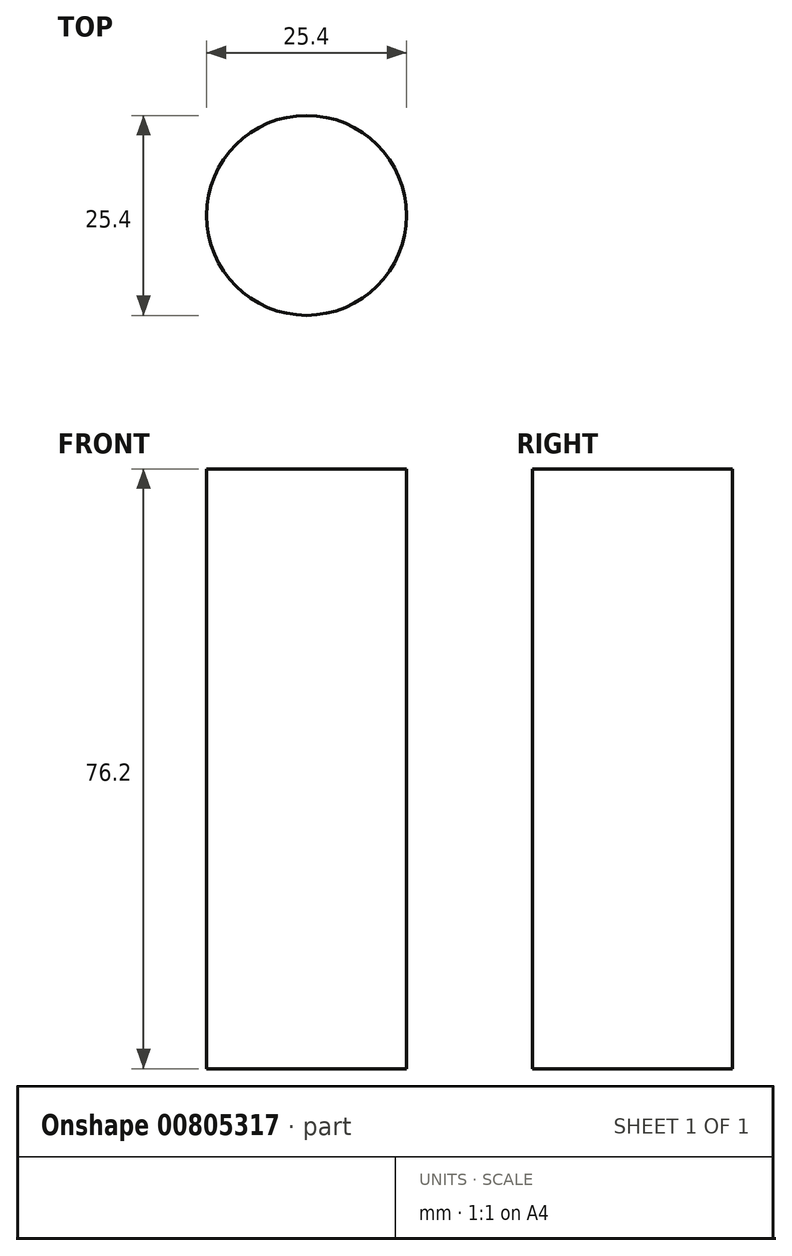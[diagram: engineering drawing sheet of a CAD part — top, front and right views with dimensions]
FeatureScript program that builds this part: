
annotation { "Feature Type Name" : "Feature", "Feature Type Description" : "" }
export const myFeature = defineFeature(function(context is Context, id is Id, definition is map)
    precondition{}
    {
        {
            var Q0;
            Q0=qCreatedBy(makeId("Front.planeOp"),FACE);
            var sketch = newSketch(context, id + "F0", { "sketchPlane" : qUnion([Q0])});
            skLineSegment(sketch, "E0", {"start": v(0, 0) * mm, "end": v(88.9, 0) * mm});
            skLineSegment(sketch, "E1", {"start": v(88.9, 0) * mm, "end": v(88.9, 1092.2) * mm});
            skLineSegment(sketch, "E2", {"start": v(88.9, 1092.2) * mm, "end": v(0, 1092.2) * mm});
            skLineSegment(sketch, "E3", {"start": v(0, 0) * mm, "end": v(0, 1191.58) * mm, "construction": true});
            skSolve(sketch);
        }
        {
            var Q0;
            Q0=qSketchRegion(id+"F0",true);
            var Q1;
            Q1=sQuery(id+"F0.wireOp",EDGE,"E1");
            var Q2;
            Q2=sQuery(id+"F0.wireOp",EDGE,"E0");
            var Q3;
            Q3=sQuery(id+"F0.wireOp",EDGE,"E2");
            var Q4;
            Q4=sQuery(id+"F0.wireOp",EDGE,"Eqfm1BcG-SU4s-36cT-mnSU-gtJC7Ga610LP");
            var Q5;
            Q5=sQuery(id+"F0.wireOp",EDGE,"Ojjtict1-wwqD-w4ix-8k3J-fVzUUkNspiEs");
            var Q6;
            Q6=sQuery(id+"F0.wireOp",EDGE,"E3");
            revolve(context, id + "F1", {"bodyType" : ToolBodyType.SURFACE, "entities" : qUnion([Q0]), "surfaceEntities" : qUnion([Q1, Q2, Q3, Q4, Q5]), "axis" : qUnion([Q6]), "revolveType" : RevolveType.FULL});
        }
        {
            var Q0;
            Q0=makeQuery(id+"F1.opRevolve","SWEPT_EDGE",EDGE,{"disambiguationData":[OSD([sQuery(id+"F0.wireOp",VERTEX,"E2.start")])]});
            fillet(context, id + "F2", {"entities" : qUnion([Q0]), "radius" : 76.2 * mm, "tangentPropagation" : true, "allowEdgeOverflow" : false});
        }
        {
            var Q0;
            Q0=makeQuery(id+"F1.opRevolve","SWEPT_FACE",FACE,{"disambiguationData":[OSD([sQuery(id+"F0.wireOp",EDGE,"E2")])]});
            extrude(context, id + "F3", {"entities" : qUnion([Q0]), "oppositeDirection" : true, "depth" : 76.2 * mm, "offsetDistance" : 25.4 * mm});
        }
    });
